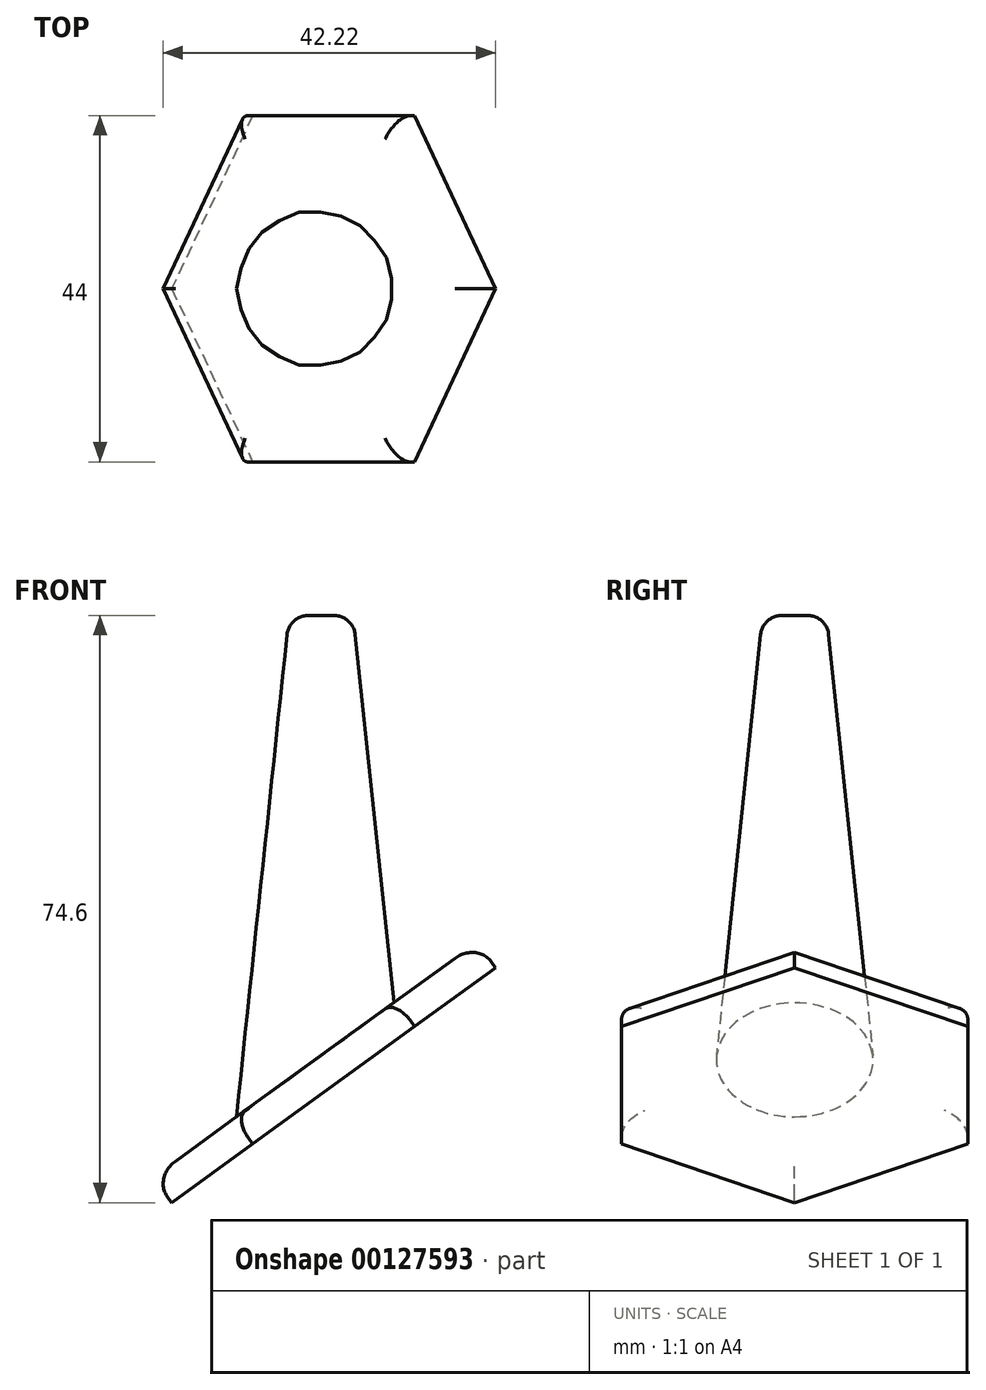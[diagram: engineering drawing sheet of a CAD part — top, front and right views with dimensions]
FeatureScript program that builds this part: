
annotation { "Feature Type Name" : "Feature", "Feature Type Description" : "" }
export const myFeature = defineFeature(function(context is Context, id is Id, definition is map)
    precondition{}
    {
        {
            var Q0;
            Q0=qCreatedBy(makeId("Front.planeOp"),FACE);
            var sketch = newSketch(context, id + "F0", { "sketchPlane" : qUnion([Q0])});
            skLineSegment(sketch, "E0", {"start": v(-11, 0) * mm, "end": v(-4.07, 66) * mm});
            skLineSegment(sketch, "E1", {"start": v(-4.07, 66) * mm, "end": v(0, 66) * mm});
            skLineSegment(sketch, "E2", {"start": v(0, 66) * mm, "end": v(0, 0) * mm});
            skLineSegment(sketch, "E3", {"start": v(0, 0) * mm, "end": v(-11, 0) * mm});
            skSolve(sketch);
        }
        {
            var Q0;
            Q0=makeQuery(id+"F0.imprint","IMPRINT",FACE,{"disambiguationData":[TD([[makeQuery(id+"F0.imprint","IMPRINT",EDGE,{"derivedFrom":sQuery(id+"F0.wireOp",EDGE,"E0")}),-1.0]])]});
            var Q1;
            Q1=sQuery(id+"F0.wireOp",EDGE,"E2");
            revolve(context, id + "F1", {"entities" : qUnion([Q0]), "axis" : qUnion([Q1]), "revolveType" : RevolveType.FULL});
        }
        {
            var Q0;
            Q0=qCreatedBy(makeId("Front.planeOp"),FACE);
            var sketch = newSketch(context, id + "F2", { "sketchPlane" : qUnion([Q0])});
            skLineSegment(sketch, "E4", {"start": v(-13.93, 0) * mm, "end": v(40.78, 39.71) * mm});
            skLineSegment(sketch, "E5", {"start": v(40.78, 39.71) * mm, "end": v(40.78, 0) * mm});
            skLineSegment(sketch, "E6", {"start": v(40.78, 0) * mm, "end": v(-13.93, 0) * mm});
            skSolve(sketch);
        }
        {
            var Q0;
            Q0 = qSketchRegion(id + "F2", true);
            extrude(context, id + "F3", {"entities" : qUnion([Q0]), "operationType" : NewBodyOperationType.REMOVE, "endBound" : BoundingType.THROUGH_ALL, "oppositeDirection" : true, "depth" : 25 * mm, "hasSecondDirection" : true, "secondDirectionBound" : SecondDirectionBoundingType.THROUGH_ALL, "secondDirectionOppositeDirection" : false, "secondDirectionDepth" : 25 * mm});
        }
        {
            var Q0;
            Q0=makeQuery(id+"F3.boolean.opBoolean","COPY",FACE,{"derivedFrom":makeQuery(id+"F3.opExtrude","SWEPT_FACE",FACE,{"disambiguationData":[OSD([sQuery(id+"F2.wireOp",EDGE,"E4")])]})});
            var sketch = newSketch(context, id + "F4", { "sketchPlane" : qUnion([Q0])});
            skCircle(sketch, "E7.cCircle", {"center": v(5, 0) * mm, "radius": 22 * mm, "construction": true});
            skPoint(sketch, "E7.cCircle.perimeterSnap0", {"position": v(5, -9.97) * mm});
            skLineSegment(sketch, "E7.0", {"start": v(17.7, -22) * mm, "end": v(-7.7, -22) * mm});
            skLineSegment(sketch, "E7.1", {"start": v(-7.7, -22) * mm, "end": v(-20.4, 0) * mm});
            skLineSegment(sketch, "E7.2", {"start": v(-20.4, 0) * mm, "end": v(-7.7, 22) * mm});
            skLineSegment(sketch, "E7.3", {"start": v(-7.7, 22) * mm, "end": v(17.7, 22) * mm});
            skLineSegment(sketch, "E7.4", {"start": v(17.7, 22) * mm, "end": v(30.4, 0) * mm});
            skLineSegment(sketch, "E7.5", {"start": v(30.4, 0) * mm, "end": v(17.7, -22) * mm});
            skPoint(sketch, "E7.0.midPoint", {"position": v(5, -22) * mm});
            skPoint(sketch, "E7.0.midPoint.positionSnap0", {"position": v(5, -9.97) * mm});
            skSolve(sketch);
        }
        {
            var Q0;
            Q0 = qSketchRegion(id + "F4", true);
            extrude(context, id + "F5", {"entities" : qUnion([Q0]), "operationType" : NewBodyOperationType.ADD, "depth" : 4 * mm});
        }
        {
            var Q0;
            Q0=makeQuery(id+"F5.opExtrude","CAP_EDGE",EDGE,{"disambiguationData":[OSD([sQuery(id+"F4.wireOp",EDGE,"E7.0")])],"isStart":true});
            var Q1;
            Q1=makeQuery(id+"F5.opExtrude","CAP_EDGE",EDGE,{"disambiguationData":[OSD([sQuery(id+"F4.wireOp",EDGE,"E7.5")])],"isStart":true});
            var Q2;
            Q2=makeQuery(id+"F5.opExtrude","CAP_EDGE",EDGE,{"disambiguationData":[OSD([sQuery(id+"F4.wireOp",EDGE,"E7.4")])],"isStart":true});
            var Q3;
            Q3=makeQuery(id+"F5.opExtrude","CAP_EDGE",EDGE,{"disambiguationData":[OSD([sQuery(id+"F4.wireOp",EDGE,"E7.3")])],"isStart":true});
            var Q4;
            Q4=makeQuery(id+"F5.opExtrude","CAP_EDGE",EDGE,{"disambiguationData":[OSD([sQuery(id+"F4.wireOp",EDGE,"E7.2")])],"isStart":true});
            var Q5;
            Q5=makeQuery(id+"F5.opExtrude","CAP_EDGE",EDGE,{"disambiguationData":[OSD([sQuery(id+"F4.wireOp",EDGE,"E7.1")])],"isStart":true});
            fillet(context, id + "F6", {"entities" : qUnion([Q0, Q1, Q2, Q3, Q4, Q5]), "radius" : 3 * mm, "tangentPropagation" : true, "allowEdgeOverflow" : false});
        }
        {
            var Q0;
            Q0=makeQuery(id+"F1.opRevolve","SWEPT_EDGE",EDGE,{"disambiguationData":[OSD([sQuery(id+"F0.wireOp",EDGE,"E0"),sQuery(id+"F0.wireOp",EDGE,"E1")])]});
            fillet(context, id + "F7", {"entities" : qUnion([Q0]), "radius" : 2.69 * mm, "tangentPropagation" : true, "allowEdgeOverflow" : false});
        }
    });
